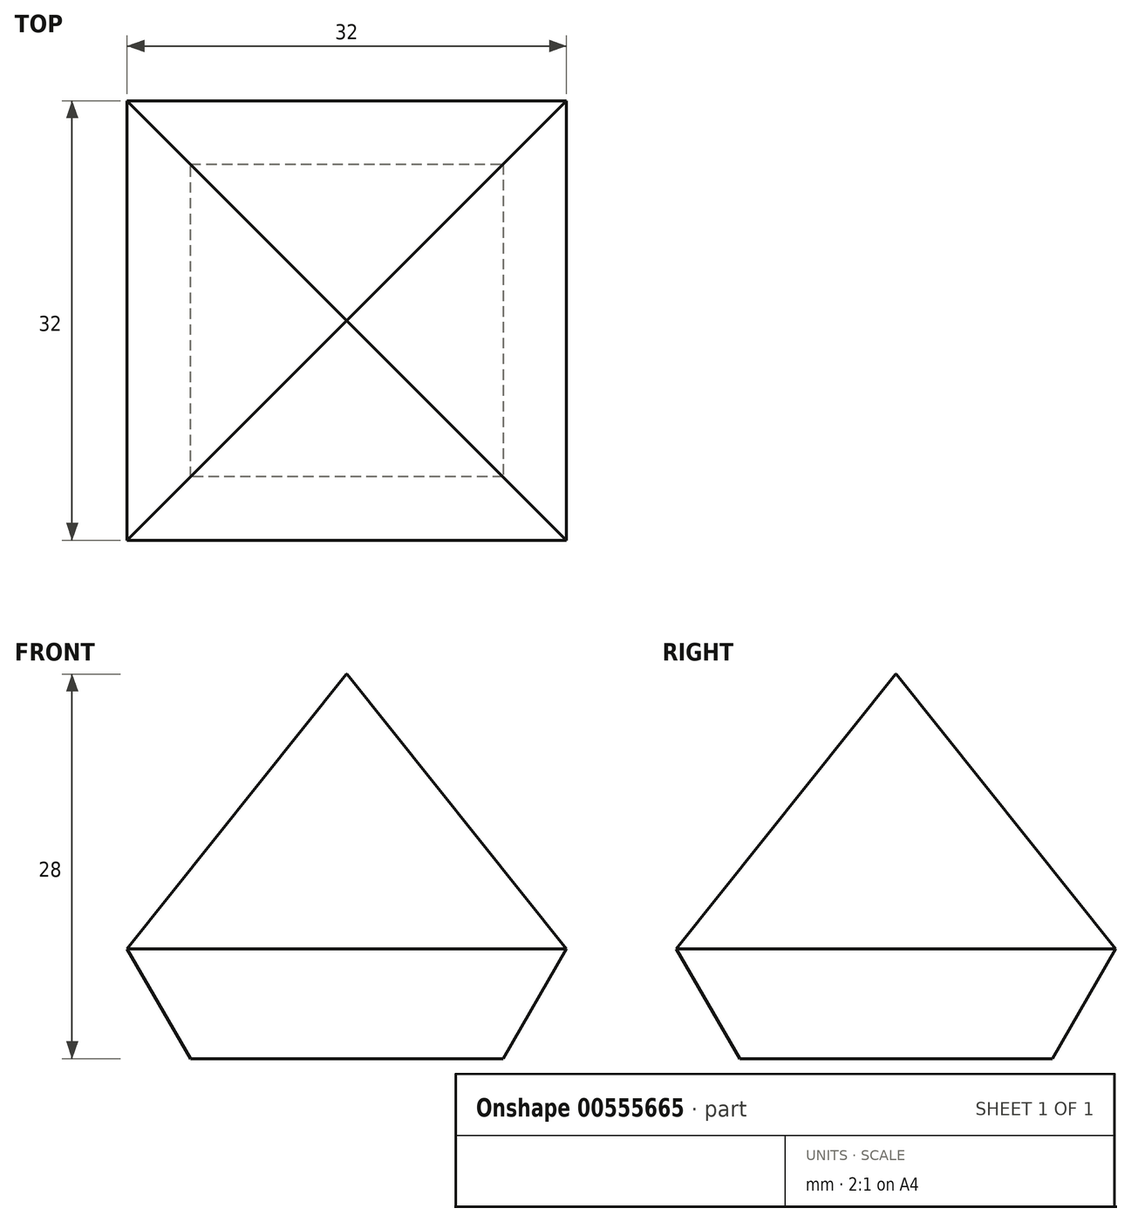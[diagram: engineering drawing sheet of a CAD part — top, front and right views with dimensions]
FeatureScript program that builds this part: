
annotation { "Feature Type Name" : "Feature", "Feature Type Description" : "" }
export const myFeature = defineFeature(function(context is Context, id is Id, definition is map)
    precondition{}
    {
        {
            var Q0;
            Q0=qCreatedBy(makeId("Front.planeOp"),FACE);
            var sketch = newSketch(context, id + "F0", { "sketchPlane" : qUnion([Q0])});
            skLineSegment(sketch, "E0", {"start": v(0, 28) * mm, "end": v(-16, 8) * mm});
            skLineSegment(sketch, "E1", {"start": v(-16, 8) * mm, "end": v(-11.38, 0) * mm});
            skLineSegment(sketch, "E2", {"start": v(-11.38, 0) * mm, "end": v(0, 0) * mm});
            skLineSegment(sketch, "E3", {"start": v(0, 0) * mm, "end": v(0, 28) * mm});
            skLineSegment(sketch, "E4", {"start": v(-16, 8) * mm, "end": v(0, 8) * mm});
            skSolve(sketch);
        }
        {
            var Q0;
            Q0=qCreatedBy(makeId("Top.planeOp"),FACE);
            var Q1;
            Q1=sQuery(id+"F0.wireOp",VERTEX,"E4.end");
            cPlane(context, id + "F1", {"entities" : qUnion([Q0, Q1]), "cplaneType" : CPlaneType.PLANE_POINT, "offset" : 25 * mm, "width" : 150 * mm, "height" : 150 * mm});
        }
        {
            var Q0;
            Q0=qCreatedBy(id+"F1.planeOp",FACE);
            var sketch = newSketch(context, id + "F2", { "sketchPlane" : qUnion([Q0])});
            skLineSegment(sketch, "E5.bottom", {"start": v(-16, -16) * mm, "end": v(16, -16) * mm});
            skLineSegment(sketch, "E5.top", {"start": v(-16, 16) * mm, "end": v(16, 16) * mm});
            skLineSegment(sketch, "E5.left", {"start": v(-16, -16) * mm, "end": v(-16, 16) * mm});
            skLineSegment(sketch, "E5.right", {"start": v(16, -16) * mm, "end": v(16, 16) * mm});
            skPoint(sketch, "E5.middle", {"position": v(0, 0) * mm});
            skSolve(sketch);
        }
        {
            var Q0;
            Q0=makeQuery(id+"F2.imprint","IMPRINT",FACE,{"disambiguationData":[TD([[makeQuery(id+"F2.imprint","IMPRINT",EDGE,{"derivedFrom":sQuery(id+"F2.wireOp",EDGE,"E5.bottom")}),1.0]])]});
            var Q1;
            Q1=sQuery(id+"F0.wireOp",VERTEX,"E3.end");
            var Q2;
            Q2=qCreatedBy(makeId("Top.planeOp"),FACE);
            extrude(context, id + "F3", {"entities" : qUnion([Q0]), "endBound" : BoundingType.UP_TO_VERTEX, "depth" : 25 * mm, "endBoundEntityVertex" : qUnion([Q1]), "offsetDistance" : 25 * mm, "hasDraft" : true, "draftAngle" : 38.6 * degree, "draftPullDirection" : true, "hasSecondDirection" : true, "secondDirectionBound" : BoundingType.UP_TO_SURFACE, "secondDirectionOppositeDirection" : true, "secondDirectionDepth" : 25 * mm, "secondDirectionBoundEntityFace" : qUnion([Q2]), "hasSecondDirectionDraft" : true, "secondDirectionDraftAngle" : 30 * degree, "secondDirectionDraftPullDirection" : true});
        }
    });
